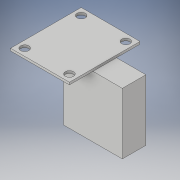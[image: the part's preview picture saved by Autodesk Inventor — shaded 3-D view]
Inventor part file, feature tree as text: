
AUTODESK INVENTOR PART (.ipt)
format: ipt  version: 2019 (Build 230136000, 136)  size: 121,856 bytes
history: native  units: in
note: dims shown in document units (in); Inventor stores cm internally (conversion verified against a paired STEP export)
features: extrude x3, sketch x3
ambient origin geometry x8: Origin, YZ Plane, XZ Plane, XY Plane, X Axis, Y Axis, Z Axis, Center Point
bodies: Solid1 (feature_tree)
feature tree (6):
  extrude  "Extrusion1"  Depth=1.25in
  extrude  "Extrusion2"  Depth=0.05in
  extrude  "Extrusion3"  Depth=0.625in
  sketch  "Sketch1"  dims[d0=1.5in d1=1.25in]
  sketch  "Sketch2"  dims[d2=0.05in d3=0.0in d4=0.15in]
  sketch  "Sketch3"  dims[d5=0.15in d6=0.175in d7=0.05in d8=0.0in d9=0.5in d10=0.5in d11=1.25in d12=1.3in d13=0.0in d14=0.625in]
